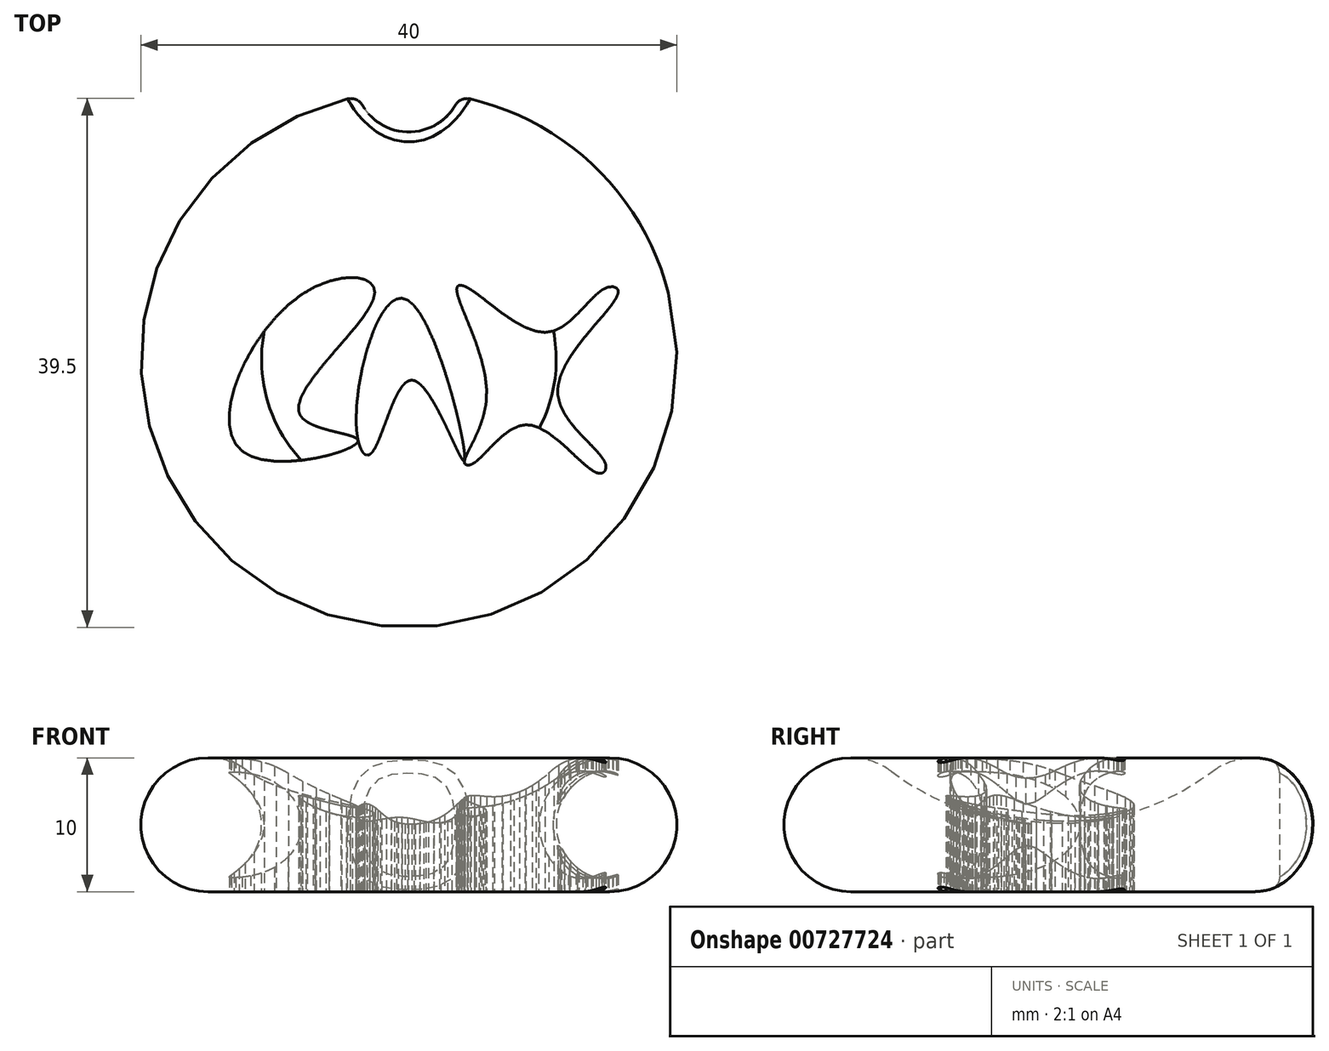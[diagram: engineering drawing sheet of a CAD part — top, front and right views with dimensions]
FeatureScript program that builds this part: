
annotation { "Feature Type Name" : "Feature", "Feature Type Description" : "" }
export const myFeature = defineFeature(function(context is Context, id is Id, definition is map)
    precondition{}
    {
        {
            var Q0;
            Q0=qCreatedBy(makeId("Front.planeOp"),FACE);
            var sketch = newSketch(context, id + "F0", { "sketchPlane" : qUnion([Q0])});
            skLineSegment(sketch, "E0", {"start": v(0, 5) * mm, "end": v(0, 0) * mm});
            skLineSegment(sketch, "E1", {"start": v(-15, 0) * mm, "end": v(0, 0) * mm});
            skArc(sketch, "E2", {"start": v(-12, 9) * mm, "mid": v(-19.74, 6.58) * mm, "end": v(-15, 0) * mm});
            skArc(sketch, "E3", {"start": v(-12, 9) * mm, "mid": v(-6.32, 6.03) * mm, "end": v(0, 5) * mm});
            skSolve(sketch);
        }
        {
            var Q0;
            Q0 = qSketchRegion(id + "F0", true);
            var Q1;
            Q1=sQuery(id+"F0.wireOp",EDGE,"E0");
            revolve(context, id + "F1", {"surfaceOperationType" : NewSurfaceOperationType.NEW, "entities" : qUnion([Q0]), "axis" : qUnion([Q1]), "revolveType" : RevolveType.FULL});
        }
        {
            var Q0;
            Q0=qCreatedBy(makeId("Top.planeOp"),FACE);
            var sketch = newSketch(context, id + "F2", { "sketchPlane" : qUnion([Q0])});
            skLineSegment(sketch, "E4", {"start": v(-3.9, -5.34) * mm, "end": v(-3.94, -4.66) * mm});
            skLineSegment(sketch, "E5", {"start": v(-3.81, -5.93) * mm, "end": v(-3.9, -5.34) * mm});
            skLineSegment(sketch, "E6", {"start": v(-3.69, -6.42) * mm, "end": v(-3.81, -5.93) * mm});
            skLineSegment(sketch, "E7", {"start": v(-3.57, -6.7) * mm, "end": v(-3.69, -6.42) * mm});
            skLineSegment(sketch, "E8", {"start": v(-3.44, -6.93) * mm, "end": v(-3.57, -6.7) * mm});
            skLineSegment(sketch, "E9", {"start": v(-3.3, -7.07) * mm, "end": v(-3.44, -6.93) * mm});
            skLineSegment(sketch, "E10", {"start": v(-3.15, -7.14) * mm, "end": v(-3.3, -7.07) * mm});
            skLineSegment(sketch, "E11", {"start": v(-2.93, -7.1) * mm, "end": v(-3.15, -7.14) * mm});
            skLineSegment(sketch, "E12", {"start": v(-2.72, -6.9) * mm, "end": v(-2.93, -7.1) * mm});
            skLineSegment(sketch, "E13", {"start": v(-2.52, -6.6) * mm, "end": v(-2.72, -6.9) * mm});
            skLineSegment(sketch, "E14", {"start": v(-2.33, -6.2) * mm, "end": v(-2.52, -6.6) * mm});
            skLineSegment(sketch, "E15", {"start": v(-2.13, -5.73) * mm, "end": v(-2.33, -6.2) * mm});
            skLineSegment(sketch, "E16", {"start": v(-1.74, -4.68) * mm, "end": v(-2.13, -5.73) * mm});
            skLineSegment(sketch, "E17", {"start": v(-1.33, -3.59) * mm, "end": v(-1.74, -4.68) * mm});
            skLineSegment(sketch, "E18", {"start": v(-1.06, -2.98) * mm, "end": v(-1.33, -3.59) * mm});
            skLineSegment(sketch, "E19", {"start": v(-0.79, -2.43) * mm, "end": v(-1.06, -2.98) * mm});
            skLineSegment(sketch, "E20", {"start": v(-0.5, -2) * mm, "end": v(-0.79, -2.43) * mm});
            skLineSegment(sketch, "E21", {"start": v(-0.27, -1.75) * mm, "end": v(-0.5, -2) * mm});
            skLineSegment(sketch, "E22", {"start": v(-0.03, -1.59) * mm, "end": v(-0.27, -1.75) * mm});
            skLineSegment(sketch, "E23", {"start": v(0.22, -1.53) * mm, "end": v(-0.03, -1.59) * mm});
            skLineSegment(sketch, "E24", {"start": v(0.48, -1.59) * mm, "end": v(0.22, -1.53) * mm});
            skLineSegment(sketch, "E25", {"start": v(0.8, -1.8) * mm, "end": v(0.48, -1.59) * mm});
            skLineSegment(sketch, "E26", {"start": v(1.12, -2.13) * mm, "end": v(0.8, -1.8) * mm});
            skLineSegment(sketch, "E27", {"start": v(1.45, -2.57) * mm, "end": v(1.12, -2.13) * mm});
            skLineSegment(sketch, "E28", {"start": v(1.87, -3.24) * mm, "end": v(1.45, -2.57) * mm});
            skLineSegment(sketch, "E29", {"start": v(2.29, -4) * mm, "end": v(1.87, -3.24) * mm});
            skLineSegment(sketch, "E30", {"start": v(2.68, -4.79) * mm, "end": v(2.29, -4) * mm});
            skLineSegment(sketch, "E31", {"start": v(3, -5.48) * mm, "end": v(2.68, -4.79) * mm});
            skLineSegment(sketch, "E32", {"start": v(3.31, -6.13) * mm, "end": v(3, -5.48) * mm});
            skLineSegment(sketch, "E33", {"start": v(3.58, -6.7) * mm, "end": v(3.31, -6.13) * mm});
            skLineSegment(sketch, "E34", {"start": v(3.73, -7) * mm, "end": v(3.58, -6.7) * mm});
            skLineSegment(sketch, "E35", {"start": v(3.86, -7.26) * mm, "end": v(3.73, -7) * mm});
            skLineSegment(sketch, "E36", {"start": v(3.99, -7.46) * mm, "end": v(3.86, -7.26) * mm});
            skLineSegment(sketch, "E37", {"start": v(4.05, -7.53) * mm, "end": v(3.99, -7.46) * mm});
            skLineSegment(sketch, "E38", {"start": v(4.1, -7.57) * mm, "end": v(4.05, -7.53) * mm});
            skLineSegment(sketch, "E39", {"start": v(4.13, -7.56) * mm, "end": v(4.1, -7.57) * mm});
            skLineSegment(sketch, "E40", {"start": v(4.15, -7.54) * mm, "end": v(4.13, -7.56) * mm});
            skLineSegment(sketch, "E41", {"start": v(4.17, -7.4) * mm, "end": v(4.15, -7.54) * mm});
            skLineSegment(sketch, "E42", {"start": v(4.16, -7.07) * mm, "end": v(4.17, -7.4) * mm});
            skLineSegment(sketch, "E43", {"start": v(4.09, -6.48) * mm, "end": v(4.16, -7.07) * mm});
            skLineSegment(sketch, "E44", {"start": v(3.95, -5.71) * mm, "end": v(4.09, -6.48) * mm});
            skLineSegment(sketch, "E45", {"start": v(3.76, -4.8) * mm, "end": v(3.95, -5.71) * mm});
            skLineSegment(sketch, "E46", {"start": v(3.51, -3.77) * mm, "end": v(3.76, -4.8) * mm});
            skLineSegment(sketch, "E47", {"start": v(3.22, -2.67) * mm, "end": v(3.51, -3.77) * mm});
            skLineSegment(sketch, "E48", {"start": v(2.9, -1.54) * mm, "end": v(3.22, -2.67) * mm});
            skLineSegment(sketch, "E49", {"start": v(2.4, -0.02) * mm, "end": v(2.9, -1.54) * mm});
            skLineSegment(sketch, "E50", {"start": v(1.85, 1.4) * mm, "end": v(2.4, -0.02) * mm});
            skLineSegment(sketch, "E51", {"start": v(1.28, 2.66) * mm, "end": v(1.85, 1.4) * mm});
            skLineSegment(sketch, "E52", {"start": v(0.83, 3.45) * mm, "end": v(1.28, 2.66) * mm});
            skLineSegment(sketch, "E53", {"start": v(0.37, 4.05) * mm, "end": v(0.83, 3.45) * mm});
            skLineSegment(sketch, "E54", {"start": v(-3.4, 3.2) * mm, "end": v(-2.95, 3.88) * mm});
            skLineSegment(sketch, "E55", {"start": v(-3.95, 2.48) * mm, "end": v(-3.4, 3.2) * mm});
            skLineSegment(sketch, "E56", {"start": v(-4.6, 1.71) * mm, "end": v(-3.95, 2.48) * mm});
            skLineSegment(sketch, "E57", {"start": v(-5.27, 0.93) * mm, "end": v(-4.6, 1.71) * mm});
            skLineSegment(sketch, "E58", {"start": v(-6.18, -0.13) * mm, "end": v(-5.27, 0.93) * mm});
            skLineSegment(sketch, "E59", {"start": v(-7.02, -1.17) * mm, "end": v(-6.18, -0.13) * mm});
            skLineSegment(sketch, "E60", {"start": v(-7.7, -2.15) * mm, "end": v(-7.02, -1.17) * mm});
            skLineSegment(sketch, "E61", {"start": v(-8.05, -2.83) * mm, "end": v(-7.7, -2.15) * mm});
            skLineSegment(sketch, "E62", {"start": v(-8.23, -3.44) * mm, "end": v(-8.05, -2.83) * mm});
            skLineSegment(sketch, "E63", {"start": v(-8.24, -3.8) * mm, "end": v(-8.23, -3.44) * mm});
            skLineSegment(sketch, "E64", {"start": v(-8.14, -4.11) * mm, "end": v(-8.24, -3.8) * mm});
            skLineSegment(sketch, "E65", {"start": v(-7.94, -4.39) * mm, "end": v(-8.14, -4.11) * mm});
            skLineSegment(sketch, "E66", {"start": v(-4.2, -5.74) * mm, "end": v(-4.65, -5.6) * mm});
            skLineSegment(sketch, "E67", {"start": v(-3.9, -5.89) * mm, "end": v(-4.2, -5.74) * mm});
            skLineSegment(sketch, "E68", {"start": v(-3.8, -6) * mm, "end": v(-3.9, -5.89) * mm});
            skLineSegment(sketch, "E69", {"start": v(-3.8, -6.15) * mm, "end": v(-3.8, -6) * mm});
            skLineSegment(sketch, "E70", {"start": v(-4.65, -5.6) * mm, "end": v(-5.27, -5.45) * mm});
            skLineSegment(sketch, "E71", {"start": v(-5.27, -5.45) * mm, "end": v(-5.95, -5.28) * mm});
            skLineSegment(sketch, "E72", {"start": v(-5.95, -5.28) * mm, "end": v(-6.64, -5.08) * mm});
            skLineSegment(sketch, "E73", {"start": v(-6.64, -5.08) * mm, "end": v(-7.15, -4.9) * mm});
            skLineSegment(sketch, "E74", {"start": v(-7.15, -4.9) * mm, "end": v(-7.59, -4.66) * mm});
            skLineSegment(sketch, "E75", {"start": v(-7.59, -4.66) * mm, "end": v(-7.94, -4.39) * mm});
            skLineSegment(sketch, "E76", {"start": v(-2.95, 3.88) * mm, "end": v(-2.65, 4.5) * mm});
            skLineSegment(sketch, "E77", {"start": v(-2.65, 4.5) * mm, "end": v(-2.54, 5.02) * mm});
            skLineSegment(sketch, "E78", {"start": v(-2.54, 5.02) * mm, "end": v(-2.64, 5.45) * mm});
            skLineSegment(sketch, "E79", {"start": v(-2.64, 5.45) * mm, "end": v(-2.92, 5.77) * mm});
            skLineSegment(sketch, "E80", {"start": v(-2.92, 5.77) * mm, "end": v(-3.3, 5.98) * mm});
            skLineSegment(sketch, "E81", {"start": v(-3.3, 5.98) * mm, "end": v(-3.8, 6.1) * mm});
            skLineSegment(sketch, "E82", {"start": v(-3.8, 6.1) * mm, "end": v(-4.37, 6.13) * mm});
            skLineSegment(sketch, "E83", {"start": v(-4.37, 6.13) * mm, "end": v(-5.02, 6.07) * mm});
            skLineSegment(sketch, "E84", {"start": v(-5.02, 6.07) * mm, "end": v(-5.97, 5.85) * mm});
            skLineSegment(sketch, "E85", {"start": v(-5.97, 5.85) * mm, "end": v(-6.97, 5.45) * mm});
            skLineSegment(sketch, "E86", {"start": v(-6.97, 5.45) * mm, "end": v(-7.98, 4.88) * mm});
            skLineSegment(sketch, "E87", {"start": v(-3.94, -4.66) * mm, "end": v(-3.9, -3.42) * mm});
            skLineSegment(sketch, "E88", {"start": v(-3.9, -3.42) * mm, "end": v(-3.74, -2.05) * mm});
            skLineSegment(sketch, "E89", {"start": v(-3.74, -2.05) * mm, "end": v(-3.48, -0.63) * mm});
            skLineSegment(sketch, "E90", {"start": v(-3.48, -0.63) * mm, "end": v(-3.12, 0.77) * mm});
            skLineSegment(sketch, "E91", {"start": v(-3.12, 0.77) * mm, "end": v(-2.68, 2.05) * mm});
            skLineSegment(sketch, "E92", {"start": v(-2.68, 2.05) * mm, "end": v(-2.37, 2.76) * mm});
            skLineSegment(sketch, "E93", {"start": v(-2.37, 2.76) * mm, "end": v(-2.04, 3.39) * mm});
            skLineSegment(sketch, "E94", {"start": v(-2.04, 3.39) * mm, "end": v(-1.68, 3.9) * mm});
            skLineSegment(sketch, "E95", {"start": v(-1.68, 3.9) * mm, "end": v(-1.31, 4.28) * mm});
            skLineSegment(sketch, "E96", {"start": v(-1.31, 4.28) * mm, "end": v(-0.93, 4.52) * mm});
            skLineSegment(sketch, "E97", {"start": v(-0.93, 4.52) * mm, "end": v(-0.53, 4.59) * mm});
            skLineSegment(sketch, "E98", {"start": v(-0.53, 4.59) * mm, "end": v(-0.08, 4.44) * mm});
            skLineSegment(sketch, "E99", {"start": v(-0.08, 4.44) * mm, "end": v(0.37, 4.05) * mm});
            skLineSegment(sketch, "E100", {"start": v(4.38, 5.38) * mm, "end": v(4.92, 5.03) * mm});
            skLineSegment(sketch, "E101", {"start": v(4.92, 5.03) * mm, "end": v(5.55, 4.56) * mm});
            skLineSegment(sketch, "E102", {"start": v(5.55, 4.56) * mm, "end": v(6.25, 4.01) * mm});
            skLineSegment(sketch, "E103", {"start": v(6.25, 4.01) * mm, "end": v(7, 3.44) * mm});
            skLineSegment(sketch, "E104", {"start": v(7, 3.44) * mm, "end": v(7.83, 2.88) * mm});
            skLineSegment(sketch, "E105", {"start": v(7.83, 2.88) * mm, "end": v(8.66, 2.42) * mm});
            skLineSegment(sketch, "E106", {"start": v(8.66, 2.42) * mm, "end": v(9.5, 2.11) * mm});
            skLineSegment(sketch, "E107", {"start": v(9.5, 2.11) * mm, "end": v(10.17, 2.03) * mm});
            skLineSegment(sketch, "E108", {"start": v(10.17, 2.03) * mm, "end": v(10.81, 2.14) * mm});
            skLineSegment(sketch, "E109", {"start": v(10.81, 2.14) * mm, "end": v(11.41, 2.42) * mm});
            skLineSegment(sketch, "E110", {"start": v(11.41, 2.42) * mm, "end": v(11.98, 2.84) * mm});
            skLineSegment(sketch, "E111", {"start": v(11.98, 2.84) * mm, "end": v(12.69, 3.5) * mm});
            skLineSegment(sketch, "E112", {"start": v(12.69, 3.5) * mm, "end": v(13.35, 4.22) * mm});
            skLineSegment(sketch, "E113", {"start": v(13.35, 4.22) * mm, "end": v(13.97, 4.85) * mm});
            skLineSegment(sketch, "E114", {"start": v(13.97, 4.85) * mm, "end": v(14.41, 5.2) * mm});
            skLineSegment(sketch, "E115", {"start": v(14.41, 5.2) * mm, "end": v(14.85, 5.4) * mm});
            skLineSegment(sketch, "E116", {"start": v(14.85, 5.4) * mm, "end": v(15.24, 5.45) * mm});
            skLineSegment(sketch, "E117", {"start": v(15.24, 5.45) * mm, "end": v(15.52, 5.33) * mm});
            skLineSegment(sketch, "E118", {"start": v(15.52, 5.33) * mm, "end": v(15.62, 5.18) * mm});
            skLineSegment(sketch, "E119", {"start": v(15.62, 5.18) * mm, "end": v(15.62, 4.96) * mm});
            skLineSegment(sketch, "E120", {"start": v(15.62, 4.96) * mm, "end": v(15.49, 4.62) * mm});
            skLineSegment(sketch, "E121", {"start": v(15.49, 4.62) * mm, "end": v(15.22, 4.2) * mm});
            skLineSegment(sketch, "E122", {"start": v(15.22, 4.2) * mm, "end": v(14.93, 3.82) * mm});
            skLineSegment(sketch, "E123", {"start": v(14.93, 3.82) * mm, "end": v(14.59, 3.4) * mm});
            skLineSegment(sketch, "E124", {"start": v(14.59, 3.4) * mm, "end": v(13.89, 2.59) * mm});
            skLineSegment(sketch, "E125", {"start": v(13.89, 2.59) * mm, "end": v(13.14, 1.7) * mm});
            skLineSegment(sketch, "E126", {"start": v(13.14, 1.7) * mm, "end": v(12.58, 0.97) * mm});
            skLineSegment(sketch, "E127", {"start": v(12.58, 0.97) * mm, "end": v(12.07, 0.24) * mm});
            skLineSegment(sketch, "E128", {"start": v(12.07, 0.24) * mm, "end": v(11.63, -0.5) * mm});
            skLineSegment(sketch, "E129", {"start": v(11.63, -0.5) * mm, "end": v(11.31, -1.25) * mm});
            skLineSegment(sketch, "E130", {"start": v(11.31, -1.25) * mm, "end": v(11.13, -1.97) * mm});
            skLineSegment(sketch, "E131", {"start": v(11.13, -1.97) * mm, "end": v(11.12, -2.68) * mm});
            skLineSegment(sketch, "E132", {"start": v(11.12, -2.68) * mm, "end": v(11.29, -3.36) * mm});
            skLineSegment(sketch, "E133", {"start": v(11.29, -3.36) * mm, "end": v(11.6, -4) * mm});
            skLineSegment(sketch, "E134", {"start": v(11.6, -4) * mm, "end": v(12, -4.62) * mm});
            skLineSegment(sketch, "E135", {"start": v(12, -4.62) * mm, "end": v(12.47, -5.2) * mm});
            skLineSegment(sketch, "E136", {"start": v(12.47, -5.2) * mm, "end": v(12.98, -5.75) * mm});
            skLineSegment(sketch, "E137", {"start": v(12.98, -5.75) * mm, "end": v(13.62, -6.4) * mm});
            skLineSegment(sketch, "E138", {"start": v(13.62, -6.4) * mm, "end": v(14.18, -7) * mm});
            skLineSegment(sketch, "E139", {"start": v(14.18, -7) * mm, "end": v(14.57, -7.54) * mm});
            skLineSegment(sketch, "E140", {"start": v(14.57, -7.54) * mm, "end": v(14.69, -7.81) * mm});
            skLineSegment(sketch, "E141", {"start": v(14.69, -7.81) * mm, "end": v(14.71, -8.06) * mm});
            skLineSegment(sketch, "E142", {"start": v(14.71, -8.06) * mm, "end": v(14.66, -8.27) * mm});
            skLineSegment(sketch, "E143", {"start": v(14.66, -8.27) * mm, "end": v(14.54, -8.42) * mm});
            skLineSegment(sketch, "E144", {"start": v(14.54, -8.42) * mm, "end": v(14.39, -8.5) * mm});
            skLineSegment(sketch, "E145", {"start": v(14.39, -8.5) * mm, "end": v(14.2, -8.5) * mm});
            skLineSegment(sketch, "E146", {"start": v(14.2, -8.5) * mm, "end": v(13.99, -8.44) * mm});
            skLineSegment(sketch, "E147", {"start": v(13.99, -8.44) * mm, "end": v(13.75, -8.32) * mm});
            skLineSegment(sketch, "E148", {"start": v(13.75, -8.32) * mm, "end": v(13.2, -7.9) * mm});
            skLineSegment(sketch, "E149", {"start": v(13.2, -7.9) * mm, "end": v(12.58, -7.35) * mm});
            skLineSegment(sketch, "E150", {"start": v(12.58, -7.35) * mm, "end": v(11.9, -6.7) * mm});
            skLineSegment(sketch, "E151", {"start": v(11.9, -6.7) * mm, "end": v(11.18, -6.07) * mm});
            skLineSegment(sketch, "E152", {"start": v(11.18, -6.07) * mm, "end": v(10.43, -5.5) * mm});
            skLineSegment(sketch, "E153", {"start": v(10.43, -5.5) * mm, "end": v(9.69, -5.08) * mm});
            skLineSegment(sketch, "E154", {"start": v(9.69, -5.08) * mm, "end": v(9.2, -4.91) * mm});
            skLineSegment(sketch, "E155", {"start": v(9.2, -4.91) * mm, "end": v(8.72, -4.87) * mm});
            skLineSegment(sketch, "E156", {"start": v(8.72, -4.87) * mm, "end": v(8.25, -4.95) * mm});
            skLineSegment(sketch, "E157", {"start": v(8.25, -4.95) * mm, "end": v(7.59, -5.26) * mm});
            skLineSegment(sketch, "E158", {"start": v(7.59, -5.26) * mm, "end": v(6.96, -5.73) * mm});
            skLineSegment(sketch, "E159", {"start": v(6.96, -5.73) * mm, "end": v(6.37, -6.28) * mm});
            skLineSegment(sketch, "E160", {"start": v(6.37, -6.28) * mm, "end": v(5.83, -6.84) * mm});
            skLineSegment(sketch, "E161", {"start": v(5.83, -6.84) * mm, "end": v(5.33, -7.34) * mm});
            skLineSegment(sketch, "E162", {"start": v(5.33, -7.34) * mm, "end": v(4.9, -7.71) * mm});
            skLineSegment(sketch, "E163", {"start": v(4.9, -7.71) * mm, "end": v(4.63, -7.85) * mm});
            skLineSegment(sketch, "E164", {"start": v(4.63, -7.85) * mm, "end": v(4.4, -7.9) * mm});
            skLineSegment(sketch, "E165", {"start": v(4.4, -7.9) * mm, "end": v(4.18, -7.82) * mm});
            skLineSegment(sketch, "E166", {"start": v(4.18, -7.82) * mm, "end": v(4.14, -7.64) * mm});
            skLineSegment(sketch, "E167", {"start": v(4.14, -7.64) * mm, "end": v(4.2, -7.38) * mm});
            skLineSegment(sketch, "E168", {"start": v(4.2, -7.38) * mm, "end": v(4.34, -7.04) * mm});
            skLineSegment(sketch, "E169", {"start": v(4.34, -7.04) * mm, "end": v(4.55, -6.62) * mm});
            skLineSegment(sketch, "E170", {"start": v(4.55, -6.62) * mm, "end": v(4.9, -5.95) * mm});
            skLineSegment(sketch, "E171", {"start": v(4.9, -5.95) * mm, "end": v(5.24, -5.16) * mm});
            skLineSegment(sketch, "E172", {"start": v(5.24, -5.16) * mm, "end": v(5.55, -4.27) * mm});
            skLineSegment(sketch, "E173", {"start": v(5.55, -4.27) * mm, "end": v(5.76, -3.3) * mm});
            skLineSegment(sketch, "E174", {"start": v(5.76, -3.3) * mm, "end": v(5.81, -2.26) * mm});
            skLineSegment(sketch, "E175", {"start": v(5.81, -2.26) * mm, "end": v(5.69, -1.17) * mm});
            skLineSegment(sketch, "E176", {"start": v(5.69, -1.17) * mm, "end": v(5.43, -0.06) * mm});
            skLineSegment(sketch, "E177", {"start": v(5.43, -0.06) * mm, "end": v(5.02, 1.2) * mm});
            skLineSegment(sketch, "E178", {"start": v(5.02, 1.2) * mm, "end": v(4.57, 2.4) * mm});
            skLineSegment(sketch, "E179", {"start": v(4.57, 2.4) * mm, "end": v(4.13, 3.48) * mm});
            skLineSegment(sketch, "E180", {"start": v(4.13, 3.48) * mm, "end": v(3.82, 4.25) * mm});
            skLineSegment(sketch, "E181", {"start": v(3.82, 4.25) * mm, "end": v(3.62, 4.86) * mm});
            skLineSegment(sketch, "E182", {"start": v(3.62, 4.86) * mm, "end": v(3.57, 5.25) * mm});
            skLineSegment(sketch, "E183", {"start": v(3.57, 5.25) * mm, "end": v(3.62, 5.45) * mm});
            skLineSegment(sketch, "E184", {"start": v(3.62, 5.45) * mm, "end": v(3.73, 5.54) * mm});
            skLineSegment(sketch, "E185", {"start": v(3.73, 5.54) * mm, "end": v(3.9, 5.55) * mm});
            skLineSegment(sketch, "E186", {"start": v(3.9, 5.55) * mm, "end": v(4.12, 5.5) * mm});
            skLineSegment(sketch, "E187", {"start": v(4.12, 5.5) * mm, "end": v(4.38, 5.38) * mm});
            skLineSegment(sketch, "E188", {"start": v(-7.98, 4.88) * mm, "end": v(-8.98, 4.11) * mm});
            skLineSegment(sketch, "E189", {"start": v(-8.98, 4.11) * mm, "end": v(-9.92, 3.19) * mm});
            skLineSegment(sketch, "E190", {"start": v(-9.92, 3.19) * mm, "end": v(-10.78, 2.14) * mm});
            skLineSegment(sketch, "E191", {"start": v(-10.78, 2.14) * mm, "end": v(-11.56, 1.01) * mm});
            skLineSegment(sketch, "E192", {"start": v(-11.56, 1.01) * mm, "end": v(-12.23, -0.17) * mm});
            skLineSegment(sketch, "E193", {"start": v(-12.23, -0.17) * mm, "end": v(-12.68, -1.17) * mm});
            skLineSegment(sketch, "E194", {"start": v(-12.68, -1.17) * mm, "end": v(-13.04, -2.16) * mm});
            skLineSegment(sketch, "E195", {"start": v(-13.04, -2.16) * mm, "end": v(-13.28, -3.13) * mm});
            skLineSegment(sketch, "E196", {"start": v(-13.28, -3.13) * mm, "end": v(-13.4, -4.04) * mm});
            skLineSegment(sketch, "E197", {"start": v(-13.4, -4.04) * mm, "end": v(-13.4, -4.9) * mm});
            skLineSegment(sketch, "E198", {"start": v(-13.4, -4.9) * mm, "end": v(-13.24, -5.66) * mm});
            skLineSegment(sketch, "E199", {"start": v(-13.24, -5.66) * mm, "end": v(-12.93, -6.3) * mm});
            skLineSegment(sketch, "E200", {"start": v(-12.93, -6.3) * mm, "end": v(-12.45, -6.83) * mm});
            skLineSegment(sketch, "E201", {"start": v(-12.45, -6.83) * mm, "end": v(-11.8, -7.22) * mm});
            skLineSegment(sketch, "E202", {"start": v(-11.8, -7.22) * mm, "end": v(-11, -7.46) * mm});
            skLineSegment(sketch, "E203", {"start": v(-11, -7.46) * mm, "end": v(-10.04, -7.59) * mm});
            skLineSegment(sketch, "E204", {"start": v(-10.04, -7.59) * mm, "end": v(-9, -7.6) * mm});
            skLineSegment(sketch, "E205", {"start": v(-9, -7.6) * mm, "end": v(-7.94, -7.52) * mm});
            skLineSegment(sketch, "E206", {"start": v(-7.94, -7.52) * mm, "end": v(-6.9, -7.36) * mm});
            skLineSegment(sketch, "E207", {"start": v(-6.9, -7.36) * mm, "end": v(-5.95, -7.14) * mm});
            skLineSegment(sketch, "E208", {"start": v(-5.95, -7.14) * mm, "end": v(-5.07, -6.87) * mm});
            skLineSegment(sketch, "E209", {"start": v(-5.07, -6.87) * mm, "end": v(-4.38, -6.58) * mm});
            skLineSegment(sketch, "E210", {"start": v(-4.38, -6.58) * mm, "end": v(-3.97, -6.33) * mm});
            skLineSegment(sketch, "E211", {"start": v(-3.97, -6.33) * mm, "end": v(-3.8, -6.15) * mm});
            skSolve(sketch);
        }
        {
            var Q0;
            Q0 = qSketchRegion(id + "F2", true);
            extrude(context, id + "F3", {"entities" : qUnion([Q0]), "operationType" : NewBodyOperationType.REMOVE, "depth" : 32 * mm, "offsetDistance" : 25.4 * mm});
        }
        {
            var Q0;
            Q0=qCreatedBy(makeId("Front.planeOp"),FACE);
            var sketch = newSketch(context, id + "F4", { "sketchPlane" : qUnion([Q0])});
            skCircle(sketch, "E212", {"center": v(-15, 5) * mm, "radius": 4 * mm});
            skSolve(sketch);
        }
        {
            var Q0;
            Q0 = qSketchRegion(id + "F4", true);
            var Q1;
            Q1=sQuery(id+"F0.wireOp",EDGE,"E0");
            revolve(context, id + "F5", {"operationType" : NewBodyOperationType.ADD, "surfaceOperationType" : NewSurfaceOperationType.NEW, "entities" : qUnion([Q0]), "axis" : qUnion([Q1]), "revolveType" : RevolveType.FULL});
        }
        {
            var Q0;
            Q0=qCreatedBy(makeId("Top.planeOp"),FACE);
            var sketch = newSketch(context, id + "F6", { "sketchPlane" : qUnion([Q0])});
            skCircle(sketch, "E213", {"center": v(0, 21) * mm, "radius": 4 * mm});
            skSolve(sketch);
        }
        {
            var Q0;
            Q0 = qSketchRegion(id + "F6", true);
            extrude(context, id + "F7", {"entities" : qUnion([Q0]), "operationType" : NewBodyOperationType.REMOVE, "depth" : 40.4 * mm, "offsetDistance" : 25.4 * mm});
        }
        {
            var Q0;
            Q0=makeQuery(id+"F7.boolean.opBoolean","INTERSECT",EDGE,{"derivedFrom":[makeQuery(id+"F1.opRevolve","SWEPT_FACE",FACE,{"disambiguationData":[OSD([sQuery(id+"F0.wireOp",EDGE,"E2")])]}),makeQuery(id+"F7.opExtrude","SWEPT_FACE",FACE,{"disambiguationData":[OSD([sQuery(id+"F6.wireOp",EDGE,"E213")])]})]});
            fillet(context, id + "F8", {"entities" : qUnion([Q0]), "radius" : 1 * mm, "tangentPropagation" : true, "allowEdgeOverflow" : false});
        }
    });
